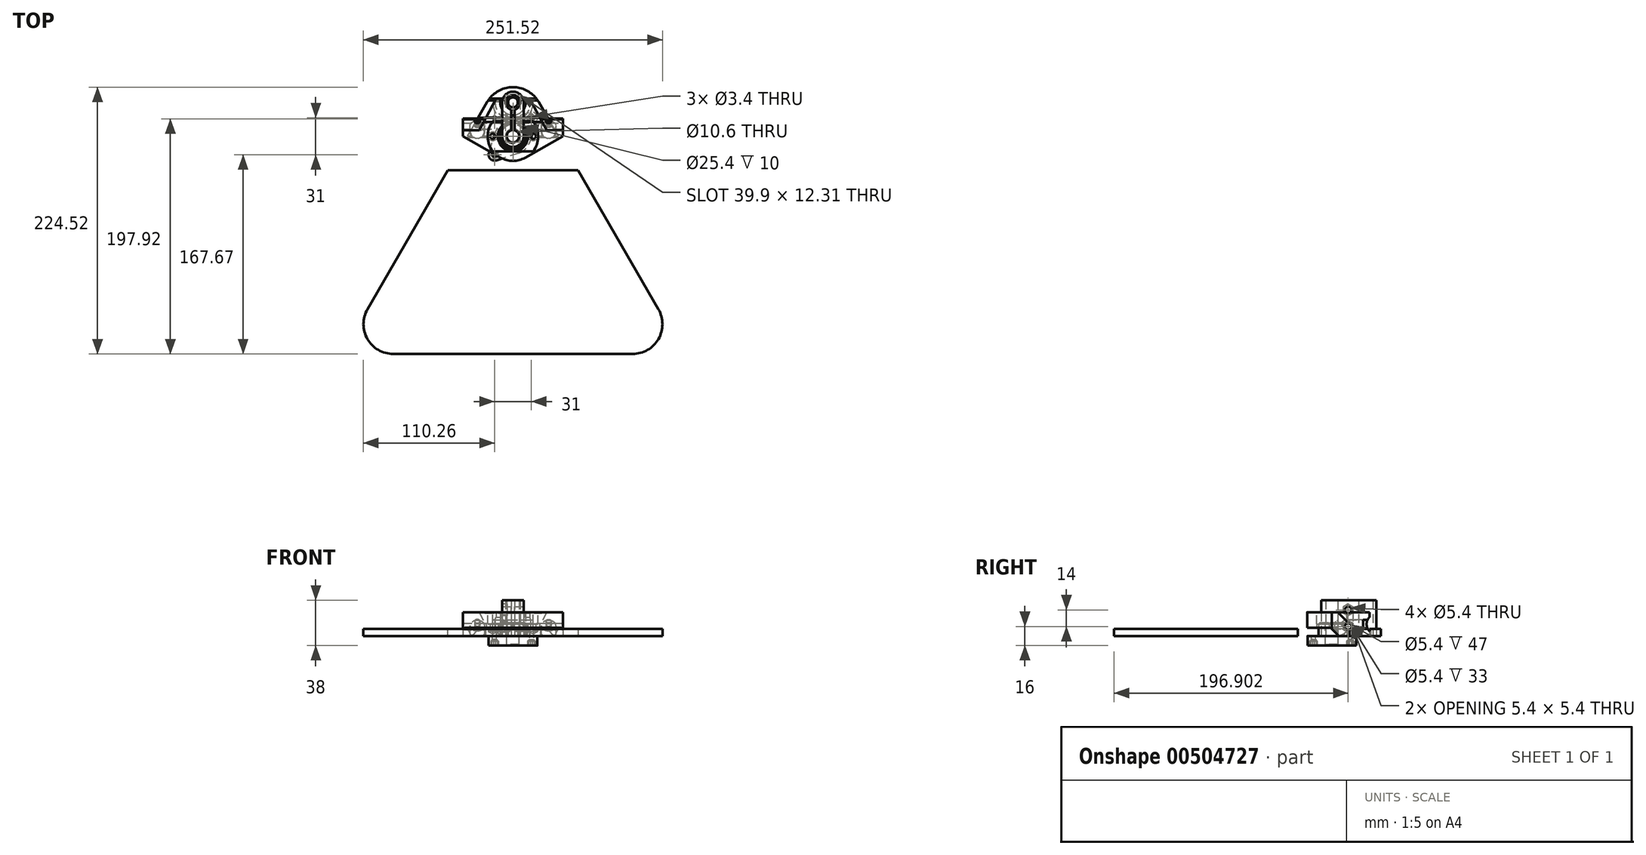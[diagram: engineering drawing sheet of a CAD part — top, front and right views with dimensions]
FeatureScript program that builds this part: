
annotation { "Feature Type Name" : "Feature", "Feature Type Description" : "" }
export const myFeature = defineFeature(function(context is Context, id is Id, definition is map)
    precondition{}
    {
        {
            var Q0;
            Q0=qCreatedBy(makeId("Top.planeOp"),FACE);
            var sketch = newSketch(context, id + "F0", { "sketchPlane" : qUnion([Q0])});
            skCircle(sketch, "E0.cCircle", {"center": v(0, 100) * mm, "radius": 15.5 * mm, "construction": true});
            skLineSegment(sketch, "E0.0", {"start": v(15.5, 115.5) * mm, "end": v(15.5, 84.5) * mm, "construction": true});
            skLineSegment(sketch, "E0.1", {"start": v(15.5, 84.5) * mm, "end": v(-15.5, 84.5) * mm, "construction": true});
            skLineSegment(sketch, "E0.2", {"start": v(-15.5, 84.5) * mm, "end": v(-15.5, 115.5) * mm, "construction": true});
            skLineSegment(sketch, "E0.3", {"start": v(-15.5, 115.5) * mm, "end": v(15.5, 115.5) * mm, "construction": true});
            skPoint(sketch, "E0.0.midPoint", {"position": v(15.5, 100) * mm});
            skCircle(sketch, "E1", {"center": v(0, 100) * mm, "radius": 11.1 * mm});
            skCircle(sketch, "E2", {"center": v(-15.5, 115.5) * mm, "radius": 1.7 * mm});
            skCircle(sketch, "E3", {"center": v(15.5, 115.5) * mm, "radius": 1.7 * mm});
            skCircle(sketch, "E4", {"center": v(15.5, 84.5) * mm, "radius": 1.7 * mm});
            skCircle(sketch, "E5", {"center": v(-15.5, 84.5) * mm, "radius": 1.7 * mm});
            skCircle(sketch, "E6.cCircle", {"center": v(0, 128.5) * mm, "radius": 6.5 * mm, "construction": true});
            skLineSegment(sketch, "E6.0", {"start": v(3.75, 122) * mm, "end": v(-3.75, 122) * mm, "construction": true});
            skLineSegment(sketch, "E6.1", {"start": v(-3.75, 122) * mm, "end": v(-7.5, 128.5) * mm, "construction": true});
            skLineSegment(sketch, "E6.2", {"start": v(-7.5, 128.5) * mm, "end": v(-3.75, 135) * mm, "construction": true});
            skLineSegment(sketch, "E6.3", {"start": v(-3.75, 135) * mm, "end": v(3.75, 135) * mm, "construction": true});
            skLineSegment(sketch, "E6.4", {"start": v(3.75, 135) * mm, "end": v(7.5, 128.5) * mm, "construction": true});
            skLineSegment(sketch, "E6.5", {"start": v(7.5, 128.5) * mm, "end": v(3.75, 122) * mm, "construction": true});
            skPoint(sketch, "E6.0.midPoint", {"position": v(0, 122) * mm});
            skCircle(sketch, "E7", {"center": v(0, 128.5) * mm, "radius": 4.1 * mm});
            skSolve(sketch);
        }
        {
            var Q0;
            Q0=qCreatedBy(makeId("Top.planeOp"),FACE);
            var sketch = newSketch(context, id + "F1", { "sketchPlane" : qUnion([Q0])});
            skCircle(sketch, "E8.cCircle", {"center": v(0, 0) * mm, "radius": 83.17 * mm, "construction": true});
            skLineSegment(sketch, "E8.0", {"start": v(144.06, -83.17) * mm, "end": v(-144.06, -83.17) * mm});
            skLineSegment(sketch, "E8.1", {"start": v(-144.06, -83.17) * mm, "end": v(0, 166.35) * mm});
            skLineSegment(sketch, "E8.2", {"start": v(0, 166.35) * mm, "end": v(144.06, -83.17) * mm});
            skPoint(sketch, "E8.0.midPoint", {"position": v(0, -83.17) * mm});
            skSolve(sketch);
        }
        {
            var Q0;
            Q0=qSketchRegion(id+"F1",true);
            extrude(context, id + "F2", {"entities" : qUnion([Q0]), "depth" : 6 * mm});
        }
        {
            var Q0;
            Q0=qSketchRegion(id+"F0",true);
            extrude(context, id + "F3", {"entities" : qUnion([Q0]), "operationType" : NewBodyOperationType.REMOVE, "endBound" : BoundingType.THROUGH_ALL, "depth" : 25 * mm});
        }
        {
            var Q0;
            Q0=qCreatedBy(makeId("Front.planeOp"),FACE);
            var sketch = newSketch(context, id + "F4", { "sketchPlane" : qUnion([Q0])});
            skLineSegment(sketch, "E9", {"start": v(0, 0) * mm, "end": v(0, 150.06) * mm, "construction": true});
            skSolve(sketch);
        }
        {
            var Q0;
            Q0=makeQuery(id+"F2.opExtrude","SWEPT_EDGE",EDGE,{"disambiguationData":[OSD([sQuery(id+"F1.wireOp",EDGE,"E8.0"),sQuery(id+"F1.wireOp",EDGE,"E8.1")])]});
            var Q1;
            Q1=makeQuery(id+"F2.opExtrude","SWEPT_EDGE",EDGE,{"disambiguationData":[OSD([sQuery(id+"F1.wireOp",EDGE,"E8.0"),sQuery(id+"F1.wireOp",EDGE,"E8.2")])]});
            var Q2;
            Q2=makeQuery(id+"F2.opExtrude","SWEPT_EDGE",EDGE,{"disambiguationData":[OSD([sQuery(id+"F1.wireOp",EDGE,"E8.1"),sQuery(id+"F1.wireOp",EDGE,"E8.2")])]});
            fillet(context, id + "F5", {"entities" : qUnion([Q0, Q1, Q2]), "radius" : 25 * mm, "tangentPropagation" : true, "allowEdgeOverflow" : false});
        }
        {
            var Q0;
            Q0=qCreatedBy(makeId("Top.planeOp"),FACE);
            var sketch = newSketch(context, id + "F6", { "sketchPlane" : qUnion([Q0])});
            skArc(sketch, "E10", {"start": v(-10.2, 131.73) * mm, "mid": v(0, 117.8) * mm, "end": v(10.2, 131.73) * mm});
            skCircle(sketch, "E11", {"center": v(0, 100) * mm, "radius": 12.7 * mm});
            skLineSegment(sketch, "E12", {"start": v(-17, 100) * mm, "end": v(17, 100) * mm, "construction": true});
            skCircle(sketch, "E13", {"center": v(17, 100) * mm, "radius": 2.2 * mm});
            skCircle(sketch, "E14", {"center": v(-17, 100) * mm, "radius": 2.2 * mm});
            skLineSegment(sketch, "E15", {"start": v(-30, 100) * mm, "end": v(30, 100) * mm, "construction": true});
            skArc(sketch, "E16", {"start": v(9.53, 136.9) * mm, "mid": v(0, 141.2) * mm, "end": v(-9.53, 136.9) * mm, "construction": true});
            skLineSegment(sketch, "E17", {"start": v(-30, 100) * mm, "end": v(-42, 100) * mm, "construction": true});
            skLineSegment(sketch, "E18", {"start": v(30, 100) * mm, "end": v(42, 100) * mm, "construction": true});
            skCircle(sketch, "E19", {"center": v(-30, 100) * mm, "radius": 6 * mm, "construction": true});
            skCircle(sketch, "E20", {"center": v(30, 100) * mm, "radius": 6 * mm, "construction": true});
            skLineSegment(sketch, "E21", {"start": v(-14.07, 131.73) * mm, "end": v(-42, 100) * mm, "construction": true});
            skLineSegment(sketch, "E22", {"start": v(14.07, 131.73) * mm, "end": v(42, 100) * mm, "construction": true});
            skArc(sketch, "E23", {"start": v(-10.2, 81.99) * mm, "mid": v(0, 79.3) * mm, "end": v(10.2, 81.99) * mm});
            skLineSegment(sketch, "E24", {"start": v(-10.2, 81.99) * mm, "end": v(-42, 100) * mm});
            skLineSegment(sketch, "E25", {"start": v(42, 100) * mm, "end": v(10.2, 81.99) * mm});
            skLineSegment(sketch, "E26", {"start": v(10.2, 131.73) * mm, "end": v(14.07, 131.73) * mm});
            skLineSegment(sketch, "E27", {"start": v(-10.2, 131.73) * mm, "end": v(-14.07, 131.73) * mm});
            skPoint(sketch, "E28", {"position": v(10.7, 128.5) * mm});
            skLineSegment(sketch, "E29", {"start": v(42, 100) * mm, "end": v(42, 115) * mm});
            skLineSegment(sketch, "E30", {"start": v(42, 115) * mm, "end": v(23, 115) * mm});
            skLineSegment(sketch, "E31", {"start": v(23, 115) * mm, "end": v(14.07, 131.73) * mm});
            skLineSegment(sketch, "E32", {"start": v(-42, 100) * mm, "end": v(-42, 115) * mm});
            skLineSegment(sketch, "E33", {"start": v(-42, 115) * mm, "end": v(-23, 115) * mm});
            skLineSegment(sketch, "E34", {"start": v(-23, 115) * mm, "end": v(-14.07, 131.73) * mm});
            skSolve(sketch);
        }
        {
            var Q0;
            Q0=qSketchRegion(id+"F6",true);
            extrude(context, id + "F7", {"entities" : qUnion([Q0]), "depth" : 20 * mm});
        }
        {
            var Q0;
            Q0=makeQuery(id+"F7.opExtrude","CAP_FACE",FACE,{"disambiguationData":[OSD([sQuery(id+"F6.wireOp",EDGE,"E10"),sQuery(id+"F6.wireOp",EDGE,"E11"),sQuery(id+"F6.wireOp",EDGE,"E13"),sQuery(id+"F6.wireOp",EDGE,"E14"),sQuery(id+"F6.wireOp",EDGE,"E16"),sQuery(id+"F6.wireOp",EDGE,"E21"),sQuery(id+"F6.wireOp",EDGE,"E22"),sQuery(id+"F6.wireOp",EDGE,"E23"),sQuery(id+"F6.wireOp",EDGE,"E24"),sQuery(id+"F6.wireOp",EDGE,"E25")])],"isStart":false});
            var sketch = newSketch(context, id + "F8", { "sketchPlane" : qUnion([Q0])});
            skLineSegment(sketch, "E35", {"start": v(-16.97, 87.3) * mm, "end": v(16.97, 87.3) * mm});
            skLineSegment(sketch, "E36", {"start": v(-16.97, 112.7) * mm, "end": v(16.97, 112.7) * mm});
            skArc(sketch, "E37", {"start": v(-16.97, 112.7) * mm, "mid": v(-21.2, 100) * mm, "end": v(-16.97, 87.3) * mm});
            skArc(sketch, "E38", {"start": v(16.97, 87.3) * mm, "mid": v(21.2, 100) * mm, "end": v(16.97, 112.7) * mm});
            skLineSegment(sketch, "E39", {"start": v(-16.97, 87.3) * mm, "end": v(-16.97, 112.7) * mm, "construction": true});
            skPoint(sketch, "E40", {"position": v(-16.97, 100) * mm});
            skSolve(sketch);
        }
        {
            var Q0;
            Q0=qSketchRegion(id+"F8",true);
            extrude(context, id + "F9", {"entities" : qUnion([Q0]), "operationType" : NewBodyOperationType.REMOVE, "oppositeDirection" : true, "depth" : 10 * mm});
        }
        {
            var Q0;
            Q0=qCreatedBy(makeId("Right.planeOp"),FACE);
            var Q1;
            Q1=sQuery(id+"F6.wireOp",VERTEX,"E18.start");
            cPlane(context, id + "F10", {"entities" : qUnion([Q0, Q1]), "cplaneType" : CPlaneType.PLANE_POINT, "offset" : 25 * mm, "width" : 150 * mm, "height" : 150 * mm});
        }
        {
            var Q0;
            Q0=qCreatedBy(id+"F10.planeOp",FACE);
            var sketch = newSketch(context, id + "F11", { "sketchPlane" : qUnion([Q0])});
            skLineSegment(sketch, "E41", {"start": v(100, 0) * mm, "end": v(100, 22.3) * mm, "construction": true});
            skLineSegment(sketch, "E42", {"start": v(123.17, 29.23) * mm, "end": v(76.83, -17.1) * mm, "construction": true});
            skPoint(sketch, "E43", {"position": v(100, 6.06) * mm});
            skCircle(sketch, "E44", {"center": v(100, 6.06) * mm, "radius": 5 * mm, "construction": true});
            skLineSegment(sketch, "E45", {"start": v(99.34, 11.06) * mm, "end": v(102.07, 11.06) * mm, "construction": true});
            skLineSegment(sketch, "E46", {"start": v(102.07, 11.06) * mm, "end": v(105, 8.13) * mm, "construction": true});
            skLineSegment(sketch, "E47", {"start": v(105, 8.13) * mm, "end": v(105, 5.4) * mm, "construction": true});
            skLineSegment(sketch, "E48", {"start": v(99.34, 11.06) * mm, "end": v(97.93, 12.47) * mm, "construction": true});
            skLineSegment(sketch, "E49", {"start": v(97.93, 12.47) * mm, "end": v(101.46, 16.01) * mm, "construction": true});
            skLineSegment(sketch, "E50", {"start": v(101.46, 16.01) * mm, "end": v(109.95, 7.53) * mm, "construction": true});
            skLineSegment(sketch, "E51", {"start": v(109.95, 7.53) * mm, "end": v(106.41, 3.99) * mm, "construction": true});
            skLineSegment(sketch, "E52", {"start": v(106.41, 3.99) * mm, "end": v(105, 5.4) * mm, "construction": true});
            skLineSegment(sketch, "E53", {"start": v(101.46, 16.01) * mm, "end": v(101.46, 20) * mm, "construction": true});
            skLineSegment(sketch, "E54", {"start": v(106.41, 3.99) * mm, "end": v(106.41, 0) * mm, "construction": true});
            skSolve(sketch);
        }
        {
            var Q0;
            Q0=qCreatedBy(makeId("Right.planeOp"),FACE);
            var sketch = newSketch(context, id + "F12", { "sketchPlane" : qUnion([Q0])});
            skLineSegment(sketch, "E55", {"start": v(106.06, 0) * mm, "end": v(99.06, 7) * mm});
            skLineSegment(sketch, "E56", {"start": v(99.06, 7) * mm, "end": v(71.34, 7) * mm});
            skLineSegment(sketch, "E57", {"start": v(71.34, 7) * mm, "end": v(71.34, 0) * mm});
            skLineSegment(sketch, "E58", {"start": v(71.34, 0) * mm, "end": v(106.06, 0) * mm});
            skSolve(sketch);
        }
        {
            var Q0;
            Q0=qSketchRegion(id+"F12",true);
            extrude(context, id + "F13", {"entities" : qUnion([Q0]), "operationType" : NewBodyOperationType.REMOVE, "endBound" : BoundingType.THROUGH_ALL, "oppositeDirection" : true, "depth" : 25 * mm, "hasSecondDirection" : true, "secondDirectionBound" : SecondDirectionBoundingType.THROUGH_ALL, "secondDirectionOppositeDirection" : false, "secondDirectionDepth" : 25 * mm});
        }
        {
            var Q0;
            Q0=sQuery(id+"F11.wireOp",EDGE,"E50");
            cPoint(context, id + "F14", {"entities" : qUnion([Q0]), "parameter" : 0.5});
        }
        {
            var Q0;
            Q0=qCreatedBy(id+"F14",VERTEX);
            var Q1;
            Q1=sQuery(id+"F11.wireOp",EDGE,"E42");
            cPlane(context, id + "F15", {"entities" : qUnion([Q0, Q1]), "cplaneType" : CPlaneType.LINE_POINT, "offset" : 25 * mm, "width" : 150 * mm, "height" : 150 * mm});
        }
        {
            var Q0;
            Q0=qCreatedBy(id+"F15.planeOp",FACE);
            var sketch = newSketch(context, id + "F16", { "sketchPlane" : qUnion([Q0])});
            skCircle(sketch, "E59", {"center": v(30, -70.71) * mm, "radius": 6.2 * mm});
            skCircle(sketch, "E60", {"center": v(-30, -70.71) * mm, "radius": 6.2 * mm});
            skSolve(sketch);
        }
        {
            var Q0;
            Q0=qSketchRegion(id+"F16",true);
            extrude(context, id + "F17", {"entities" : qUnion([Q0]), "operationType" : NewBodyOperationType.REMOVE, "endBound" : BoundingType.THROUGH_ALL, "depth" : 25 * mm});
        }
        {
            var Q0;
            Q0=makeQuery(id+"F7.opExtrude","CAP_EDGE",EDGE,{"disambiguationData":[OSD([sQuery(id+"F6.wireOp",EDGE,"E30")])],"isStart":false});
            var Q1;
            Q1=makeQuery(id+"F7.opExtrude","CAP_EDGE",EDGE,{"disambiguationData":[OSD([sQuery(id+"F6.wireOp",EDGE,"E33")])],"isStart":false});
            chamfer(context, id + "F18", {"entities" : qUnion([Q0, Q1]), "width" : 10 * mm, "tangentPropagation" : true});
        }
        {
            var Q0;
            Q0=qCreatedBy(id+"F15.planeOp",FACE);
            var sketch = newSketch(context, id + "F19", { "sketchPlane" : qUnion([Q0])});
            skCircle(sketch, "E61", {"center": v(-30, -70.71) * mm, "radius": 2.2 * mm});
            skCircle(sketch, "E62", {"center": v(30, -70.71) * mm, "radius": 2.2 * mm});
            skSolve(sketch);
        }
        {
            var Q0;
            Q0=qSketchRegion(id+"F19",true);
            extrude(context, id + "F20", {"entities" : qUnion([Q0]), "operationType" : NewBodyOperationType.REMOVE, "endBound" : BoundingType.THROUGH_ALL, "oppositeDirection" : true, "depth" : 25 * mm});
        }
        {
            var Q0;
            Q0=qCreatedBy(makeId("Right.planeOp"),FACE);
            var sketch = newSketch(context, id + "F21", { "sketchPlane" : qUnion([Q0])});
            skArc(sketch, "E63", {"start": v(131.73, 16) * mm, "mid": v(129.25, 10) * mm, "end": v(131.73, 4) * mm});
            skLineSegment(sketch, "E64", {"start": v(131.73, 16) * mm, "end": v(131.73, 4) * mm});
            skLineSegment(sketch, "E65", {"start": v(131.73, 16) * mm, "end": v(131.73, 20) * mm, "construction": true});
            skLineSegment(sketch, "E66", {"start": v(131.73, 4) * mm, "end": v(131.73, 0) * mm, "construction": true});
            skLineSegment(sketch, "E67", {"start": v(137.73, 10) * mm, "end": v(131.73, 16) * mm, "construction": true});
            skSolve(sketch);
        }
        {
            var Q0;
            Q0=qSketchRegion(id+"F21",true);
            extrude(context, id + "F22", {"entities" : qUnion([Q0]), "operationType" : NewBodyOperationType.REMOVE, "endBound" : BoundingType.THROUGH_ALL, "oppositeDirection" : true, "depth" : 25 * mm, "hasSecondDirection" : true, "secondDirectionBound" : SecondDirectionBoundingType.THROUGH_ALL, "secondDirectionOppositeDirection" : false, "secondDirectionDepth" : 25 * mm});
        }
        {
            var Q0;
            Q0=makeQuery(id+"F13.boolean.opBoolean","COPY",FACE,{"derivedFrom":makeQuery(id+"F13.opExtrude","SWEPT_FACE",FACE,{"disambiguationData":[OSD([sQuery(id+"F12.wireOp",EDGE,"E56")])]})});
            var sketch = newSketch(context, id + "F23", { "sketchPlane" : qUnion([Q0])});
            skCircle(sketch, "E68.cCircle", {"center": v(17, -100) * mm, "radius": 3.7 * mm, "construction": true});
            skLineSegment(sketch, "E68.0", {"start": v(17, -104.27) * mm, "end": v(13.3, -102.14) * mm});
            skLineSegment(sketch, "E68.1", {"start": v(13.3, -102.14) * mm, "end": v(13.3, -97.86) * mm});
            skLineSegment(sketch, "E68.2", {"start": v(13.3, -97.86) * mm, "end": v(17, -95.73) * mm});
            skLineSegment(sketch, "E68.3", {"start": v(17, -95.73) * mm, "end": v(20.7, -97.86) * mm});
            skLineSegment(sketch, "E68.4", {"start": v(20.7, -97.86) * mm, "end": v(20.7, -102.14) * mm});
            skLineSegment(sketch, "E68.5", {"start": v(20.7, -102.14) * mm, "end": v(17, -104.27) * mm});
            skPoint(sketch, "E68.0.midPoint", {"position": v(15.15, -103.2) * mm});
            skCircle(sketch, "E69.cCircle", {"center": v(-17, -100) * mm, "radius": 3.7 * mm, "construction": true});
            skLineSegment(sketch, "E69.0", {"start": v(-17, -104.27) * mm, "end": v(-20.7, -102.14) * mm});
            skLineSegment(sketch, "E69.1", {"start": v(-20.7, -102.14) * mm, "end": v(-20.7, -97.86) * mm});
            skLineSegment(sketch, "E69.2", {"start": v(-20.7, -97.86) * mm, "end": v(-17, -95.73) * mm});
            skLineSegment(sketch, "E69.3", {"start": v(-17, -95.73) * mm, "end": v(-13.3, -97.86) * mm});
            skLineSegment(sketch, "E69.4", {"start": v(-13.3, -97.86) * mm, "end": v(-13.3, -102.14) * mm});
            skLineSegment(sketch, "E69.5", {"start": v(-13.3, -102.14) * mm, "end": v(-17, -104.27) * mm});
            skPoint(sketch, "E69.0.midPoint", {"position": v(-18.85, -103.2) * mm});
            skSolve(sketch);
        }
        {
            var Q0;
            Q0=qSketchRegion(id+"F23",true);
            extrude(context, id + "F24", {"entities" : qUnion([Q0]), "operationType" : NewBodyOperationType.REMOVE, "oppositeDirection" : true, "depth" : .2 * mm, "hasSecondDirection" : true, "secondDirectionBound" : SecondDirectionBoundingType.THROUGH_ALL, "secondDirectionOppositeDirection" : false, "secondDirectionDepth" : 25 * mm});
        }
        {
            var Q0;
            Q0=qCreatedBy(makeId("Right.planeOp"),FACE);
            var sketch = newSketch(context, id + "F25", { "sketchPlane" : qUnion([Q0])});
            skLineSegment(sketch, "E70", {"start": v(128.5, 0) * mm, "end": v(128.5, 20) * mm, "construction": true});
            skLineSegment(sketch, "E71.bottom", {"start": v(111.5, 13.5) * mm, "end": v(113.5, 13.5) * mm});
            skLineSegment(sketch, "E71.top", {"start": v(111.5, 6.5) * mm, "end": v(113.5, 6.5) * mm});
            skLineSegment(sketch, "E71.left", {"start": v(111.5, 13.5) * mm, "end": v(111.5, 6.5) * mm});
            skLineSegment(sketch, "E71.right", {"start": v(113.5, 13.5) * mm, "end": v(113.5, 6.5) * mm});
            skLineSegment(sketch, "E72", {"start": v(113.5, 10) * mm, "end": v(128.5, 10) * mm, "construction": true});
            skSolve(sketch);
        }
        {
            var Q0;
            Q0=qSketchRegion(id+"F25",true);
            var Q1;
            Q1=sQuery(id+"F25.wireOp",EDGE,"E70");
            revolve(context, id + "F26", {"operationType" : NewBodyOperationType.REMOVE, "entities" : qUnion([Q0]), "axis" : qUnion([Q1]), "revolveType" : RevolveType.FULL, "oppositeDirection" : true});
        }
        {
            var Q0;
            Q0=qCreatedBy(makeId("Top.planeOp"),FACE);
            var sketch = newSketch(context, id + "F27", { "sketchPlane" : qUnion([Q0])});
            skCircle(sketch, "E73", {"center": v(0, 100) * mm, "radius": 5.3 * mm});
            skCircle(sketch, "E74", {"center": v(15.5, 115.5) * mm, "radius": 1.7 * mm});
            skCircle(sketch, "E75", {"center": v(-15.5, 84.5) * mm, "radius": 1.7 * mm});
            skArc(sketch, "E76", {"start": v(20.26, 113.97) * mm, "mid": v(19.04, 119.04) * mm, "end": v(13.97, 120.26) * mm});
            skCircle(sketch, "E77", {"center": v(0, 100) * mm, "radius": 11 * mm});
            skArc(sketch, "E78", {"start": v(-4.6, 114.28) * mm, "mid": v(-10.6, 110.6) * mm, "end": v(-14.28, 104.6) * mm});
            skArc(sketch, "E79", {"start": v(-20.26, 86.03) * mm, "mid": v(-19.04, 80.96) * mm, "end": v(-13.97, 79.74) * mm});
            skArc(sketch, "E80", {"start": v(4.6, 85.72) * mm, "mid": v(10.6, 89.4) * mm, "end": v(14.28, 95.4) * mm});
            skLineSegment(sketch, "E81", {"start": v(4.6, 85.72) * mm, "end": v(-13.97, 79.74) * mm});
            skLineSegment(sketch, "E82", {"start": v(-20.26, 86.03) * mm, "end": v(-14.28, 104.6) * mm});
            skLineSegment(sketch, "E83", {"start": v(-4.6, 114.28) * mm, "end": v(13.97, 120.26) * mm});
            skLineSegment(sketch, "E84", {"start": v(14.28, 95.4) * mm, "end": v(20.26, 113.97) * mm});
            skSolve(sketch);
        }
        {
            var Q0;
            Q0=qSketchRegion(id+"F27",true);
            var Q1;
            Q1=makeQuery(id+"F27.imprint","IMPRINT",FACE,{"disambiguationData":[TD([[makeQuery(id+"F27.imprint","IMPRINT",EDGE,{"derivedFrom":sQuery(id+"F27.wireOp",EDGE,"E73")}),-1.0]])]});
            extrude(context, id + "F28", {"entities" : qUnion([Q0, Q1]), "oppositeDirection" : true, "depth" : 8 * mm});
        }
        {
            var Q0;
            Q0=makeQuery(id+"F27.imprint","IMPRINT",FACE,{"disambiguationData":[TD([[makeQuery(id+"F27.imprint","IMPRINT",EDGE,{"derivedFrom":sQuery(id+"F27.wireOp",EDGE,"E73")}),1.0]])]});
            var Q1;
            Q1=makeQuery(id+"F0.imprint","IMPRINT",FACE,{"disambiguationData":[TD([[makeQuery(id+"F0.imprint","IMPRINT",EDGE,{"derivedFrom":sQuery(id+"F0.wireOp",EDGE,"E1")}),1.0]])]});
            extrude(context, id + "F29", {"entities" : qUnion([Q0, Q1]), "operationType" : NewBodyOperationType.ADD, "depth" : 11 * mm});
        }
        {
            var Q0;
            Q0=makeQuery(id+"F27.imprint","IMPRINT",FACE,{"disambiguationData":[TD([[makeQuery(id+"F27.imprint","IMPRINT",EDGE,{"derivedFrom":sQuery(id+"F27.wireOp",EDGE,"E73")}),1.0]])]});
            var Q1;
            Q1=sQuery(id+"F27.wireOp",EDGE,"E73");
            extrude(context, id + "F30", {"entities" : qUnion([Q0]), "operationType" : NewBodyOperationType.REMOVE, "surfaceEntities" : qUnion([Q1]), "endBound" : BoundingType.THROUGH_ALL, "depth" : 25 * mm});
        }
        {
            var Q0;
            Q0=qCreatedBy(makeId("Top.planeOp"),FACE);
            var sketch = newSketch(context, id + "F31", { "sketchPlane" : qUnion([Q0])});
            skArc(sketch, "E85", {"start": v(1.5, 122.48) * mm, "mid": v(0, 134.7) * mm, "end": v(-1.5, 122.48) * mm});
            skArc(sketch, "E86", {"start": v(-1.5, 104.98) * mm, "mid": v(0, 94.8) * mm, "end": v(1.5, 104.98) * mm});
            skArc(sketch, "E87", {"start": v(-9, 128.5) * mm, "mid": v(0, 137.5) * mm, "end": v(9, 128.5) * mm});
            skArc(sketch, "E88", {"start": v(-9, 100) * mm, "mid": v(0, 91) * mm, "end": v(9, 100) * mm});
            skLineSegment(sketch, "E89", {"start": v(9, 100) * mm, "end": v(9, 128.5) * mm});
            skLineSegment(sketch, "E90", {"start": v(-9, 128.5) * mm, "end": v(-9, 100) * mm});
            skLineSegment(sketch, "E91", {"start": v(-1.5, 122.48) * mm, "end": v(-1.5, 104.98) * mm});
            skLineSegment(sketch, "E92", {"start": v(1.5, 122.48) * mm, "end": v(1.5, 104.98) * mm});
            skSolve(sketch);
        }
        {
            var Q0;
            Q0=qSketchRegion(id+"F31",true);
            extrude(context, id + "F32", {"entities" : qUnion([Q0]), "depth" : 30 * mm});
        }
        {
            var Q0;
            Q0=qCreatedBy(makeId("Right.planeOp"),FACE);
            var sketch = newSketch(context, id + "F33", { "sketchPlane" : qUnion([Q0])});
            skCircle(sketch, "E93", {"center": v(113.73, 22) * mm, "radius": 2.7 * mm});
            skLineSegment(sketch, "E94", {"start": v(113.73, 30) * mm, "end": v(113.73, 22) * mm, "construction": true});
            skLineSegment(sketch, "E95", {"start": v(113.73, 22) * mm, "end": v(113.73, 8) * mm, "construction": true});
            skLineSegment(sketch, "E96", {"start": v(113.73, 8) * mm, "end": v(113.73, 0) * mm, "construction": true});
            skCircle(sketch, "E97", {"center": v(113.73, 8) * mm, "radius": 2.7 * mm});
            skSolve(sketch);
        }
        {
            var Q0;
            Q0=qSketchRegion(id+"F33",true);
            extrude(context, id + "F34", {"entities" : qUnion([Q0]), "operationType" : NewBodyOperationType.REMOVE, "endBound" : BoundingType.THROUGH_ALL, "oppositeDirection" : true, "depth" : 25 * mm, "hasSecondDirection" : true, "secondDirectionBound" : SecondDirectionBoundingType.THROUGH_ALL, "secondDirectionOppositeDirection" : false, "secondDirectionDepth" : 25 * mm});
        }
        {
            var Q0;
            Q0=makeQuery(id+"F32.opExtrude","SWEPT_FACE",FACE,{"disambiguationData":[OSD([sQuery(id+"F31.wireOp",EDGE,"E90")])]});
            var sketch = newSketch(context, id + "F35", { "sketchPlane" : qUnion([Q0])});
            skCircle(sketch, "E98.cCircle", {"center": v(-113.73, 22) * mm, "radius": 4.2 * mm, "construction": true});
            skLineSegment(sketch, "E98.0", {"start": v(-109.53, 24.42) * mm, "end": v(-109.53, 19.58) * mm});
            skLineSegment(sketch, "E98.1", {"start": v(-109.53, 19.58) * mm, "end": v(-113.73, 17.15) * mm});
            skLineSegment(sketch, "E98.2", {"start": v(-113.73, 17.15) * mm, "end": v(-117.93, 19.58) * mm});
            skLineSegment(sketch, "E98.3", {"start": v(-117.93, 19.58) * mm, "end": v(-117.93, 24.42) * mm});
            skLineSegment(sketch, "E98.4", {"start": v(-117.93, 24.42) * mm, "end": v(-113.73, 26.85) * mm});
            skLineSegment(sketch, "E98.5", {"start": v(-113.73, 26.85) * mm, "end": v(-109.53, 24.42) * mm});
            skPoint(sketch, "E98.0.midPoint", {"position": v(-109.53, 22) * mm});
            skCircle(sketch, "E99.cCircle", {"center": v(-113.73, 8) * mm, "radius": 4.2 * mm, "construction": true});
            skLineSegment(sketch, "E99.0", {"start": v(-109.53, 10.42) * mm, "end": v(-109.53, 5.58) * mm});
            skLineSegment(sketch, "E99.1", {"start": v(-109.53, 5.58) * mm, "end": v(-113.73, 3.15) * mm});
            skLineSegment(sketch, "E99.2", {"start": v(-113.73, 3.15) * mm, "end": v(-117.93, 5.58) * mm});
            skLineSegment(sketch, "E99.3", {"start": v(-117.93, 5.58) * mm, "end": v(-117.93, 10.42) * mm});
            skLineSegment(sketch, "E99.4", {"start": v(-117.93, 10.42) * mm, "end": v(-113.73, 12.85) * mm});
            skLineSegment(sketch, "E99.5", {"start": v(-113.73, 12.85) * mm, "end": v(-109.53, 10.42) * mm});
            skPoint(sketch, "E99.0.midPoint", {"position": v(-109.53, 8) * mm});
            skSolve(sketch);
        }
        {
            var Q0;
            Q0=qSketchRegion(id+"F35",true);
            extrude(context, id + "F36", {"entities" : qUnion([Q0]), "operationType" : NewBodyOperationType.REMOVE, "oppositeDirection" : true, "depth" : 4 * mm});
        }
        {
            var Q0;
            Q0=makeQuery(id+"F28.opExtrude","CAP_FACE",FACE,{"disambiguationData":[OSD([sQuery(id+"F27.wireOp",EDGE,"E73"),sQuery(id+"F27.wireOp",EDGE,"E74"),sQuery(id+"F27.wireOp",EDGE,"E75"),sQuery(id+"F27.wireOp",EDGE,"E76"),sQuery(id+"F27.wireOp",EDGE,"E78"),sQuery(id+"F27.wireOp",EDGE,"E79"),sQuery(id+"F27.wireOp",EDGE,"E80"),sQuery(id+"F27.wireOp",EDGE,"E81"),sQuery(id+"F27.wireOp",EDGE,"E82"),sQuery(id+"F27.wireOp",EDGE,"E83"),sQuery(id+"F27.wireOp",EDGE,"E84")])],"isStart":false});
            var sketch = newSketch(context, id + "F37", { "sketchPlane" : qUnion([Q0])});
            skCircle(sketch, "E100.cCircle", {"center": v(-15.5, -84.5) * mm, "radius": 2.85 * mm, "construction": true});
            skLineSegment(sketch, "E100.0", {"start": v(-12.32, -85.35) * mm, "end": v(-14.65, -87.68) * mm});
            skLineSegment(sketch, "E100.1", {"start": v(-14.65, -87.68) * mm, "end": v(-17.83, -86.83) * mm});
            skLineSegment(sketch, "E100.2", {"start": v(-17.83, -86.83) * mm, "end": v(-18.68, -83.65) * mm});
            skLineSegment(sketch, "E100.3", {"start": v(-18.68, -83.65) * mm, "end": v(-16.35, -81.32) * mm});
            skLineSegment(sketch, "E100.4", {"start": v(-16.35, -81.32) * mm, "end": v(-13.17, -82.17) * mm});
            skLineSegment(sketch, "E100.5", {"start": v(-13.17, -82.17) * mm, "end": v(-12.32, -85.35) * mm});
            skPoint(sketch, "E100.0.midPoint", {"position": v(-13.48, -86.52) * mm});
            skCircle(sketch, "E101.cCircle", {"center": v(15.5, -115.5) * mm, "radius": 2.85 * mm, "construction": true});
            skLineSegment(sketch, "E101.0", {"start": v(12.32, -114.65) * mm, "end": v(14.65, -112.32) * mm});
            skLineSegment(sketch, "E101.1", {"start": v(14.65, -112.32) * mm, "end": v(17.83, -113.17) * mm});
            skLineSegment(sketch, "E101.2", {"start": v(17.83, -113.17) * mm, "end": v(18.68, -116.35) * mm});
            skLineSegment(sketch, "E101.3", {"start": v(18.68, -116.35) * mm, "end": v(16.35, -118.68) * mm});
            skLineSegment(sketch, "E101.4", {"start": v(16.35, -118.68) * mm, "end": v(13.17, -117.83) * mm});
            skLineSegment(sketch, "E101.5", {"start": v(13.17, -117.83) * mm, "end": v(12.32, -114.65) * mm});
            skPoint(sketch, "E101.0.midPoint", {"position": v(13.48, -113.48) * mm});
            skLineSegment(sketch, "E102", {"start": v(-13.48, -86.52) * mm, "end": v(-15.5, -84.5) * mm, "construction": true});
            skSolve(sketch);
        }
        {
            var Q0;
            Q0=qSketchRegion(id+"F37",true);
            extrude(context, id + "F38", {"entities" : qUnion([Q0]), "operationType" : NewBodyOperationType.REMOVE, "oppositeDirection" : true, "depth" : 4 * mm});
        }
        {
            var Q0;
            Q0=makeQuery(id+"F38.boolean.opBoolean","INTERSECT",EDGE,{"derivedFrom":[makeQuery(id+"F28.opExtrude","SWEPT_FACE",FACE,{"disambiguationData":[OSD([sQuery(id+"F27.wireOp",EDGE,"E75")])]}),makeQuery(id+"F38.opExtrude","CAP_FACE",FACE,{"disambiguationData":[OSD([sQuery(id+"F37.wireOp",EDGE,"E100.0"),sQuery(id+"F37.wireOp",EDGE,"E100.1"),sQuery(id+"F37.wireOp",EDGE,"E100.2"),sQuery(id+"F37.wireOp",EDGE,"E100.3"),sQuery(id+"F37.wireOp",EDGE,"E100.4"),sQuery(id+"F37.wireOp",EDGE,"E100.5")])],"isStart":false})]});
            var Q1;
            Q1=makeQuery(id+"F38.boolean.opBoolean","INTERSECT",EDGE,{"derivedFrom":[makeQuery(id+"F28.opExtrude","SWEPT_FACE",FACE,{"disambiguationData":[OSD([sQuery(id+"F27.wireOp",EDGE,"E74")])]}),makeQuery(id+"F38.opExtrude","CAP_FACE",FACE,{"disambiguationData":[OSD([sQuery(id+"F37.wireOp",EDGE,"E101.0"),sQuery(id+"F37.wireOp",EDGE,"E101.1"),sQuery(id+"F37.wireOp",EDGE,"E101.2"),sQuery(id+"F37.wireOp",EDGE,"E101.3"),sQuery(id+"F37.wireOp",EDGE,"E101.4"),sQuery(id+"F37.wireOp",EDGE,"E101.5")])],"isStart":false})]});
            var Q2;
            Q2=makeQuery(id+"F29.opExtrude","CAP_EDGE",EDGE,{"disambiguationData":[OSD([sQuery(id+"F0.wireOp",EDGE,"E1")])],"isStart":false});
            var Q3;
            Q3=makeQuery(id+"F30.boolean.opBoolean","INTERSECT",EDGE,{"derivedFrom":[makeQuery(id+"F29.opExtrude","CAP_FACE",FACE,{"disambiguationData":[OSD([sQuery(id+"F0.wireOp",EDGE,"E1")])],"isStart":false}),makeQuery(id+"F30.opExtrude","SWEPT_FACE",FACE,{"disambiguationData":[OSD([sQuery(id+"F27.wireOp",EDGE,"E73")])]})]});
            var Q4;
            Q4=makeQuery(id+"F28.opExtrude","CAP_EDGE",EDGE,{"disambiguationData":[OSD([sQuery(id+"F27.wireOp",EDGE,"E73")])],"isStart":false});
            chamfer(context, id + "F39", {"entities" : qUnion([Q0, Q1, Q2, Q3, Q4]), "width" : 1 * mm, "tangentPropagation" : true});
        }
    });
